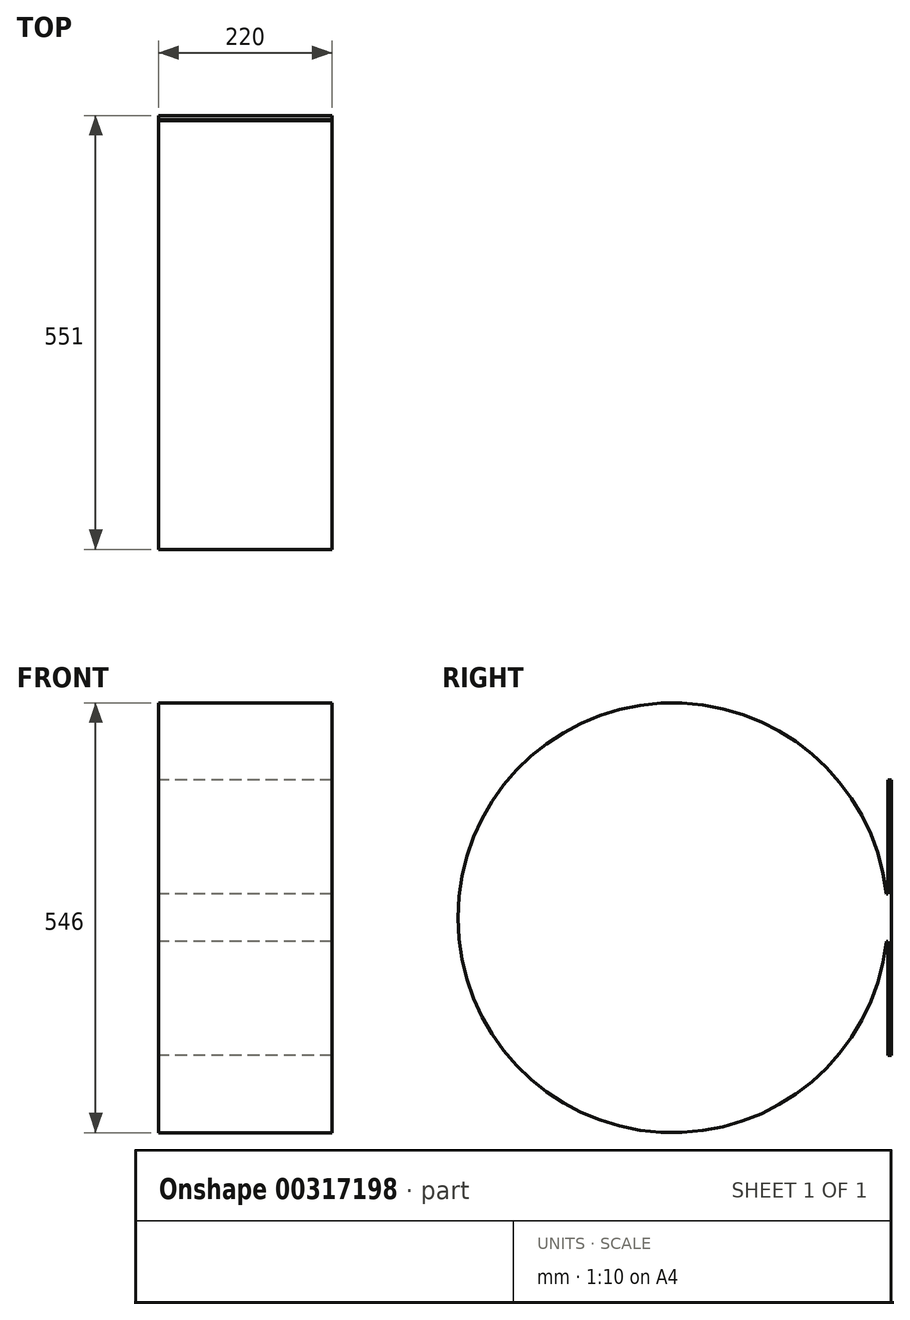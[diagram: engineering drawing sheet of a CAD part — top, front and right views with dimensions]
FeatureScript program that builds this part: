
annotation { "Feature Type Name" : "Feature", "Feature Type Description" : "" }
export const myFeature = defineFeature(function(context is Context, id is Id, definition is map)
    precondition{}
    {
        {
            var Q0;
            Q0=qCreatedBy(makeId("Right.planeOp"),FACE);
            var sketch = newSketch(context, id + "F0", { "sketchPlane" : qUnion([Q0])});
            skArc(sketch, "E0", {"start": v(-1.65, 30) * mm, "mid": v(-546, 0) * mm, "end": v(-1.65, -30) * mm});
            skLineSegment(sketch, "E1", {"start": v(-273, 0) * mm, "end": v(0, 0) * mm, "construction": true});
            skLineSegment(sketch, "E2.bottom", {"start": v(5, 175) * mm, "end": v(0, 175) * mm});
            skLineSegment(sketch, "E2.top", {"start": v(5, -175) * mm, "end": v(0, -175) * mm});
            skLineSegment(sketch, "E2.left", {"start": v(5, 175) * mm, "end": v(5, -175) * mm});
            skLineSegment(sketch, "E2.right", {"start": v(0, 175) * mm, "end": v(0, 30) * mm});
            skLineSegment(sketch, "E3", {"start": v(-1.65, 30) * mm, "end": v(0, 30) * mm});
            skLineSegment(sketch, "E4", {"start": v(-1.65, -30) * mm, "end": v(0, -30) * mm});
            skLineSegment(sketch, "E5.trimOffspring", {"start": v(0, -30) * mm, "end": v(0, -175) * mm});
            skSolve(sketch);
        }
        {
            var Q0;
            Q0 = qSketchRegion(id + "F0", true);
            extrude(context, id + "F1", {"entities" : qUnion([Q0]), "depth" : 110 * mm, "hasSecondDirection" : true, "secondDirectionOppositeDirection" : true, "secondDirectionDepth" : 110 * mm});
        }
    });
